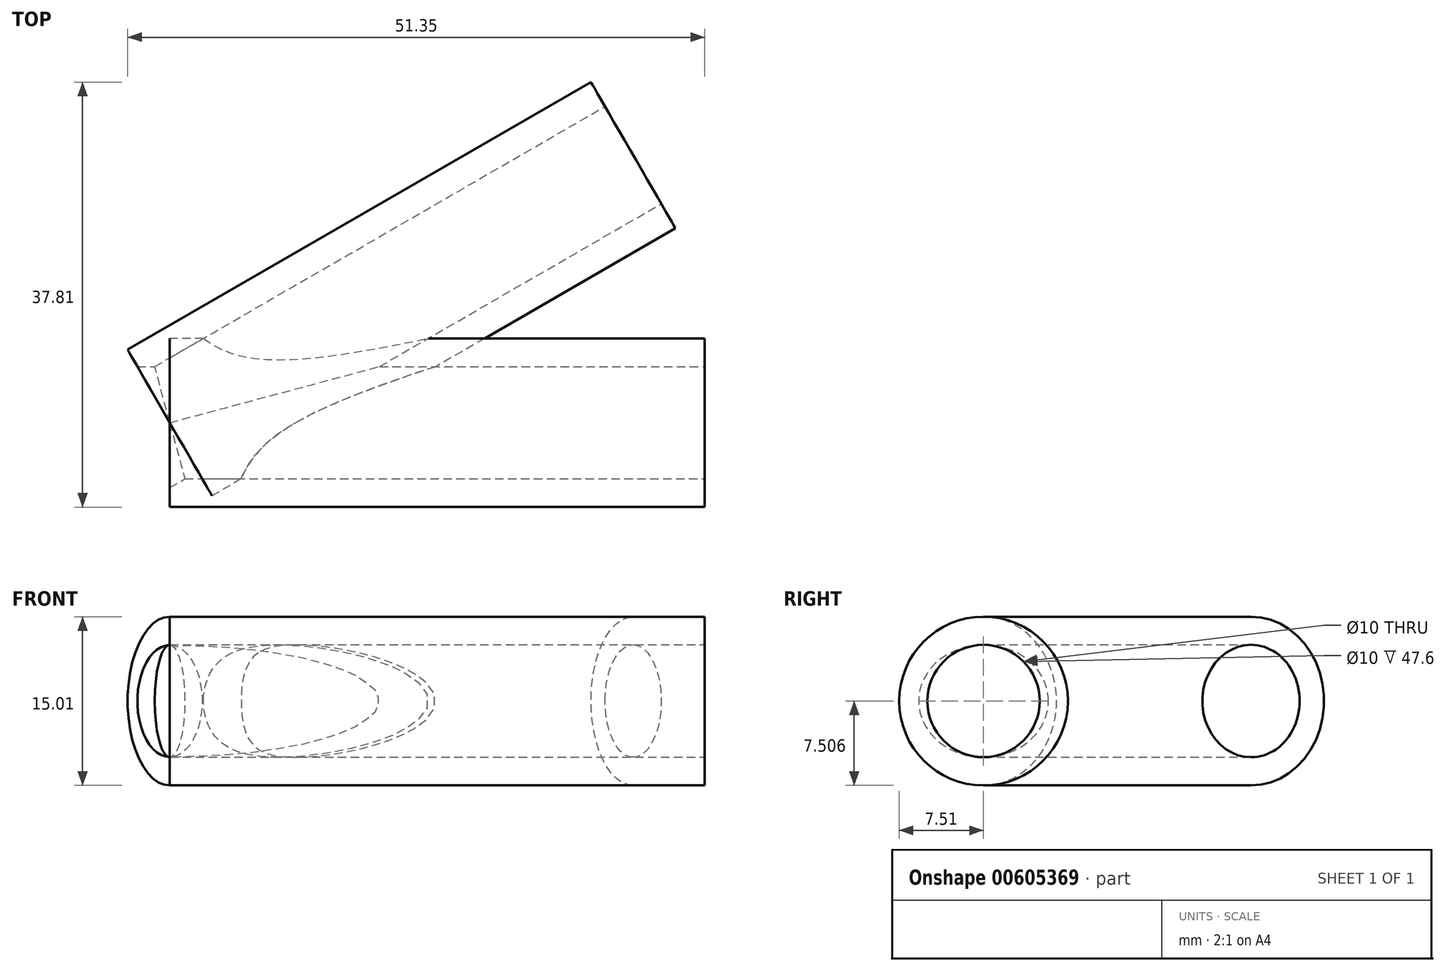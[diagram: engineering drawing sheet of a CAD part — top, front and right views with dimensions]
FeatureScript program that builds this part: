
annotation { "Feature Type Name" : "Feature", "Feature Type Description" : "" }
export const myFeature = defineFeature(function(context is Context, id is Id, definition is map)
    precondition{}
    {
        {
            var Q0;
            Q0=qCreatedBy(makeId("Right.planeOp"),FACE);
            var sketch = newSketch(context, id + "F0", { "sketchPlane" : qUnion([Q0])});
            skCircle(sketch, "E0", {"center": v(0, 17.82) * mm, "radius": 7.5 * mm});
            skSolve(sketch);
        }
        {
            var Q0;
            Q0=makeQuery(id+"F0.imprint","IMPRINT",FACE,{"disambiguationData":[TD([[makeQuery(id+"F0.imprint","IMPRINT",EDGE,{"derivedFrom":sQuery(id+"F0.wireOp",EDGE,"E0")}),1.0]])]});
            extrude(context, id + "F1", {"entities" : qUnion([Q0]), "depth" : 47.6 * mm, "offsetDistance" : 25 * mm});
        }
        {
            var Q0;
            Q0=qCreatedBy(makeId("Front.planeOp"),FACE);
            var sketch = newSketch(context, id + "F2", { "sketchPlane" : qUnion([Q0])});
            skLineSegment(sketch, "E1", {"start": v(0, 0) * mm, "end": v(0, 38.2) * mm, "construction": true});
            skSolve(sketch);
        }
        {
            var Q0;
            Q0=makeQuery(id+"F1.opExtrude","SWEPT_BODY",BODY,{"disambiguationData":[OSD([sQuery(id+"F0.wireOp",EDGE,"E0")])]});
            var Q1;
            Q1=sQuery(id+"F2.wireOp",EDGE,"E1");
            var Q2;
            Q2=sQuery(id+"F2.wireOp",EDGE,"E1");
            transform(context, id + "F3", {"entities" : qUnion([Q0]), "transformType" : TransformType.ROTATION, "transformAxis" : qUnion([Q2]), "angle" : 30 * degree, "makeCopy" : true});
        }
        {
            var Q0;
            Q0=makeQuery(id+"F1.opExtrude","CAP_FACE",FACE,{"disambiguationData":[OSD([sQuery(id+"F0.wireOp",EDGE,"E0")])],"isStart":false});
            var sketch = newSketch(context, id + "F4", { "sketchPlane" : qUnion([Q0])});
            skLineSegment(sketch, "E2", {"start": v(0, 0) * mm, "end": v(0, 28.47) * mm, "construction": true});
            skLineSegment(sketch, "E3", {"start": v(-10.41, 17.82) * mm, "end": v(15.34, 17.82) * mm, "construction": true});
            skPoint(sketch, "E4", {"position": v(0, 17.82) * mm});
            skSolve(sketch);
        }
        {
            var Q0;
            Q0=makeQuery(id+"F3.opPattern","COPY",FACE,{"derivedFrom":makeQuery(id+"F1.opExtrude","CAP_FACE",FACE,{"disambiguationData":[OSD([sQuery(id+"F0.wireOp",EDGE,"E0")])],"isStart":false}),"instanceName":"1"});
            var sketch = newSketch(context, id + "F5", { "sketchPlane" : qUnion([Q0])});
            skPoint(sketch, "E5", {"position": v(0, 17.82) * mm});
            skSolve(sketch);
        }
        {
            var Q0;
            Q0=sQuery(id+"F5.wireOp",VERTEX,"E5");
            var Q1;
            Q1=sQuery(id+"F4.wireOp",VERTEX,"E4");
            var Q2;
            Q2=makeQuery(id+"F1.opExtrude","SWEPT_BODY",BODY,{"disambiguationData":[OSD([sQuery(id+"F0.wireOp",EDGE,"E0")])]});
            var Q3;
            Q3=makeQuery(id+"F3.opPattern","COPY",BODY,{"derivedFrom":makeQuery(id+"F1.opExtrude","SWEPT_BODY",BODY,{"disambiguationData":[OSD([sQuery(id+"F0.wireOp",EDGE,"E0")])]}),"instanceName":"1"});
            hole(context, id + "F6", {"style" : HoleStyle.SIMPLE, "endStyle" : HoleEndStyle.THROUGH, "holeDiameter" : 10 * mm, "majorDiameter" : 5 * mm, "isTappedThrough" : true, "tappedDepth" : 12 * mm, "tapClearance" : 3, "startFromSketch" : true, "locations" : qUnion([Q0, Q1]), "scope" : qUnion([Q2, Q3])});
        }
    });
